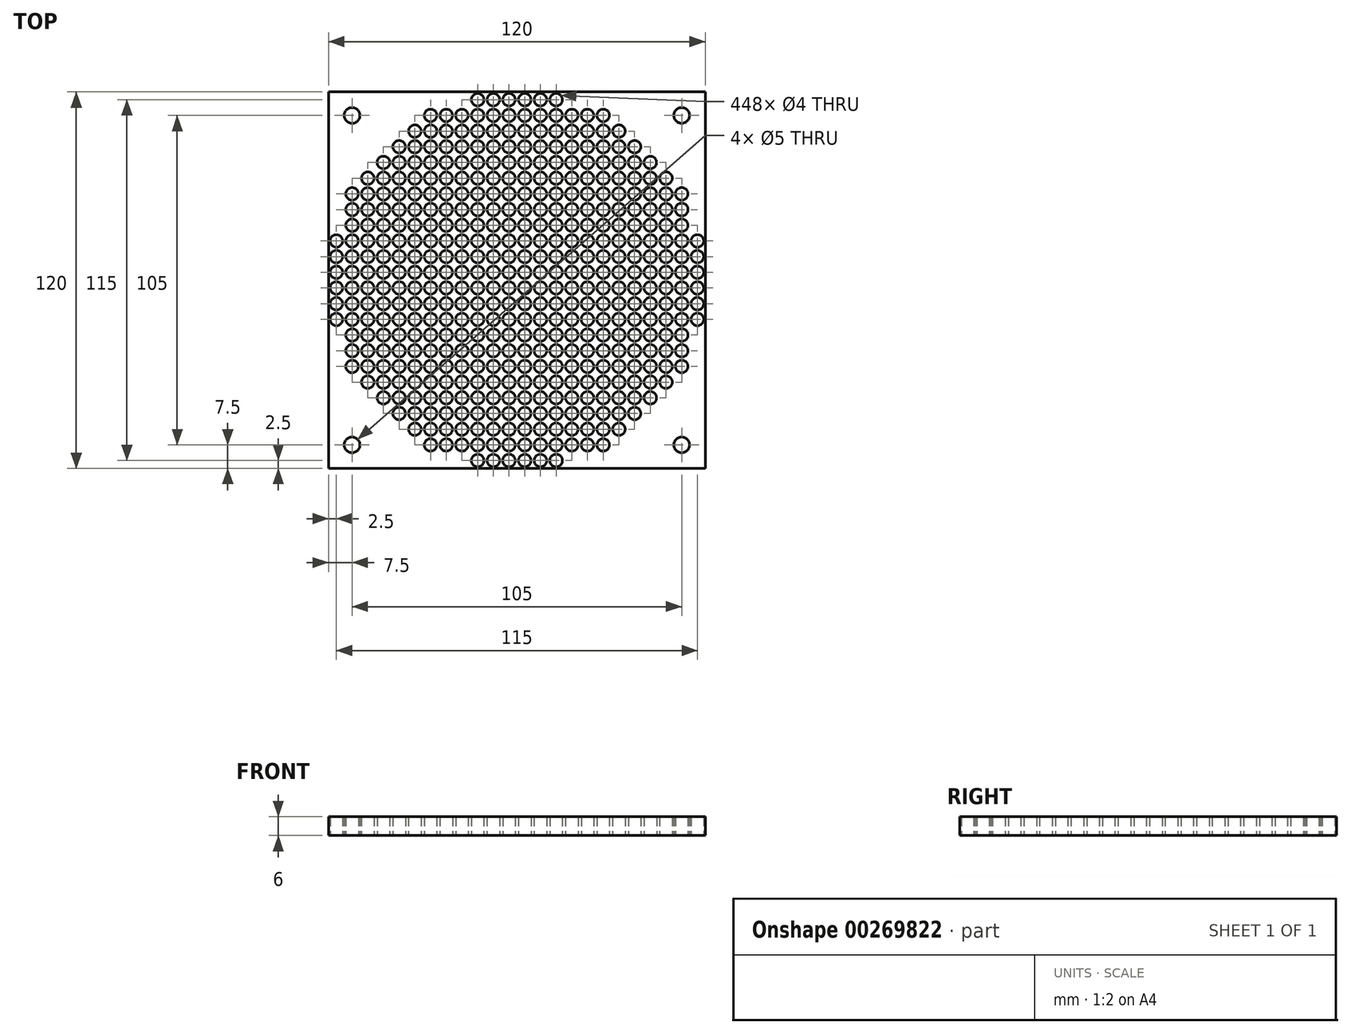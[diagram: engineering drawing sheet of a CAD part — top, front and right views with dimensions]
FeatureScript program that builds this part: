
annotation { "Feature Type Name" : "Feature", "Feature Type Description" : "" }
export const myFeature = defineFeature(function(context is Context, id is Id, definition is map)
    precondition{}
    {
        {
            var Q0;
            Q0=qCreatedBy(makeId("Top.planeOp"),FACE);
            var sketch = newSketch(context, id + "F0", { "sketchPlane" : qUnion([Q0])});
            skLineSegment(sketch, "E0", {"start": v(-60, 60) * mm, "end": v(0, 60) * mm});
            skLineSegment(sketch, "E1", {"start": v(-60, 60) * mm, "end": v(-60, 0) * mm});
            skLineSegment(sketch, "E2.MirrorCS", {"start": v(60, 60) * mm, "end": v(0, 60) * mm});
            skLineSegment(sketch, "E3.MirrorCS", {"start": v(60, 60) * mm, "end": v(60, 0) * mm});
            skLineSegment(sketch, "E4.MirrorCS", {"start": v(-60, -60) * mm, "end": v(-60, 0) * mm});
            skLineSegment(sketch, "E5.MirrorCS", {"start": v(-60, -60) * mm, "end": v(0, -60) * mm});
            skLineSegment(sketch, "E6.MirrorCS", {"start": v(60, -60) * mm, "end": v(0, -60) * mm});
            skLineSegment(sketch, "E7.MirrorCS", {"start": v(60, -60) * mm, "end": v(60, 0) * mm});
            skCircle(sketch, "E8", {"center": v(-52.5, 52.5) * mm, "radius": 2.5 * mm});
            skCircle(sketch, "E9.MirrorC", {"center": v(52.5, 52.5) * mm, "radius": 2.5 * mm});
            skCircle(sketch, "E10.MirrorC", {"center": v(-52.5, -52.5) * mm, "radius": 2.5 * mm});
            skCircle(sketch, "E11.MirrorC", {"center": v(52.5, -52.5) * mm, "radius": 2.5 * mm});
            skCircle(sketch, "E12", {"center": v(-2.5, 2.5) * mm, "radius": 2 * mm});
            skCircle(sketch, "E13.0.1.0", {"center": v(-2.5, 7.5) * mm, "radius": 2 * mm});
            skCircle(sketch, "E13.0.2.0", {"center": v(-2.5, 12.5) * mm, "radius": 2 * mm});
            skCircle(sketch, "E13.0.3.0", {"center": v(-2.5, 17.5) * mm, "radius": 2 * mm});
            skCircle(sketch, "E13.0.4.0", {"center": v(-2.5, 22.5) * mm, "radius": 2 * mm});
            skCircle(sketch, "E13.0.5.0", {"center": v(-2.5, 27.5) * mm, "radius": 2 * mm});
            skCircle(sketch, "E13.0.6.0", {"center": v(-2.5, 32.5) * mm, "radius": 2 * mm});
            skCircle(sketch, "E13.0.7.0", {"center": v(-2.5, 37.5) * mm, "radius": 2 * mm});
            skCircle(sketch, "E13.0.8.0", {"center": v(-2.5, 42.5) * mm, "radius": 2 * mm});
            skCircle(sketch, "E13.0.9.0", {"center": v(-2.5, 47.5) * mm, "radius": 2 * mm});
            skCircle(sketch, "E13.0.10.0", {"center": v(-2.5, 52.5) * mm, "radius": 2 * mm});
            skCircle(sketch, "E13.0.11.0", {"center": v(-2.5, 57.5) * mm, "radius": 2 * mm});
            skCircle(sketch, "E13.1.0.0", {"center": v(-7.5, 2.5) * mm, "radius": 2 * mm});
            skCircle(sketch, "E13.1.1.0", {"center": v(-7.5, 7.5) * mm, "radius": 2 * mm});
            skCircle(sketch, "E13.1.2.0", {"center": v(-7.5, 12.5) * mm, "radius": 2 * mm});
            skCircle(sketch, "E13.1.3.0", {"center": v(-7.5, 17.5) * mm, "radius": 2 * mm});
            skCircle(sketch, "E13.1.4.0", {"center": v(-7.5, 22.5) * mm, "radius": 2 * mm});
            skCircle(sketch, "E13.1.5.0", {"center": v(-7.5, 27.5) * mm, "radius": 2 * mm});
            skCircle(sketch, "E13.1.6.0", {"center": v(-7.5, 32.5) * mm, "radius": 2 * mm});
            skCircle(sketch, "E13.1.7.0", {"center": v(-7.5, 37.5) * mm, "radius": 2 * mm});
            skCircle(sketch, "E13.1.8.0", {"center": v(-7.5, 42.5) * mm, "radius": 2 * mm});
            skCircle(sketch, "E13.1.9.0", {"center": v(-7.5, 47.5) * mm, "radius": 2 * mm});
            skCircle(sketch, "E13.1.10.0", {"center": v(-7.5, 52.5) * mm, "radius": 2 * mm});
            skCircle(sketch, "E13.1.11.0", {"center": v(-7.5, 57.5) * mm, "radius": 2 * mm});
            skCircle(sketch, "E13.2.0.0", {"center": v(-12.5, 2.5) * mm, "radius": 2 * mm});
            skCircle(sketch, "E13.2.1.0", {"center": v(-12.5, 7.5) * mm, "radius": 2 * mm});
            skCircle(sketch, "E13.2.2.0", {"center": v(-12.5, 12.5) * mm, "radius": 2 * mm});
            skCircle(sketch, "E13.2.3.0", {"center": v(-12.5, 17.5) * mm, "radius": 2 * mm});
            skCircle(sketch, "E13.2.4.0", {"center": v(-12.5, 22.5) * mm, "radius": 2 * mm});
            skCircle(sketch, "E13.2.5.0", {"center": v(-12.5, 27.5) * mm, "radius": 2 * mm});
            skCircle(sketch, "E13.2.6.0", {"center": v(-12.5, 32.5) * mm, "radius": 2 * mm});
            skCircle(sketch, "E13.2.7.0", {"center": v(-12.5, 37.5) * mm, "radius": 2 * mm});
            skCircle(sketch, "E13.2.8.0", {"center": v(-12.5, 42.5) * mm, "radius": 2 * mm});
            skCircle(sketch, "E13.2.9.0", {"center": v(-12.5, 47.5) * mm, "radius": 2 * mm});
            skCircle(sketch, "E13.2.10.0", {"center": v(-12.5, 52.5) * mm, "radius": 2 * mm});
            skCircle(sketch, "E13.2.11.0", {"center": v(-12.5, 57.5) * mm, "radius": 2 * mm});
            skCircle(sketch, "E13.3.0.0", {"center": v(-17.5, 2.5) * mm, "radius": 2 * mm});
            skCircle(sketch, "E13.3.1.0", {"center": v(-17.5, 7.5) * mm, "radius": 2 * mm});
            skCircle(sketch, "E13.3.2.0", {"center": v(-17.5, 12.5) * mm, "radius": 2 * mm});
            skCircle(sketch, "E13.3.3.0", {"center": v(-17.5, 17.5) * mm, "radius": 2 * mm});
            skCircle(sketch, "E13.3.4.0", {"center": v(-17.5, 22.5) * mm, "radius": 2 * mm});
            skCircle(sketch, "E13.3.5.0", {"center": v(-17.5, 27.5) * mm, "radius": 2 * mm});
            skCircle(sketch, "E13.3.6.0", {"center": v(-17.5, 32.5) * mm, "radius": 2 * mm});
            skCircle(sketch, "E13.3.7.0", {"center": v(-17.5, 37.5) * mm, "radius": 2 * mm});
            skCircle(sketch, "E13.3.8.0", {"center": v(-17.5, 42.5) * mm, "radius": 2 * mm});
            skCircle(sketch, "E13.3.9.0", {"center": v(-17.5, 47.5) * mm, "radius": 2 * mm});
            skCircle(sketch, "E13.3.10.0", {"center": v(-17.5, 52.5) * mm, "radius": 2 * mm});
            skCircle(sketch, "E13.4.0.0", {"center": v(-22.5, 2.5) * mm, "radius": 2 * mm});
            skCircle(sketch, "E13.4.1.0", {"center": v(-22.5, 7.5) * mm, "radius": 2 * mm});
            skCircle(sketch, "E13.4.2.0", {"center": v(-22.5, 12.5) * mm, "radius": 2 * mm});
            skCircle(sketch, "E13.4.3.0", {"center": v(-22.5, 17.5) * mm, "radius": 2 * mm});
            skCircle(sketch, "E13.4.4.0", {"center": v(-22.5, 22.5) * mm, "radius": 2 * mm});
            skCircle(sketch, "E13.4.5.0", {"center": v(-22.5, 27.5) * mm, "radius": 2 * mm});
            skCircle(sketch, "E13.4.6.0", {"center": v(-22.5, 32.5) * mm, "radius": 2 * mm});
            skCircle(sketch, "E13.4.7.0", {"center": v(-22.5, 37.5) * mm, "radius": 2 * mm});
            skCircle(sketch, "E13.4.8.0", {"center": v(-22.5, 42.5) * mm, "radius": 2 * mm});
            skCircle(sketch, "E13.4.9.0", {"center": v(-22.5, 47.5) * mm, "radius": 2 * mm});
            skCircle(sketch, "E13.4.10.0", {"center": v(-22.5, 52.5) * mm, "radius": 2 * mm});
            skCircle(sketch, "E13.5.0.0", {"center": v(-27.5, 2.5) * mm, "radius": 2 * mm});
            skCircle(sketch, "E13.5.1.0", {"center": v(-27.5, 7.5) * mm, "radius": 2 * mm});
            skCircle(sketch, "E13.5.2.0", {"center": v(-27.5, 12.5) * mm, "radius": 2 * mm});
            skCircle(sketch, "E13.5.3.0", {"center": v(-27.5, 17.5) * mm, "radius": 2 * mm});
            skCircle(sketch, "E13.5.4.0", {"center": v(-27.5, 22.5) * mm, "radius": 2 * mm});
            skCircle(sketch, "E13.5.5.0", {"center": v(-27.5, 27.5) * mm, "radius": 2 * mm});
            skCircle(sketch, "E13.5.6.0", {"center": v(-27.5, 32.5) * mm, "radius": 2 * mm});
            skCircle(sketch, "E13.5.7.0", {"center": v(-27.5, 37.5) * mm, "radius": 2 * mm});
            skCircle(sketch, "E13.5.8.0", {"center": v(-27.5, 42.5) * mm, "radius": 2 * mm});
            skCircle(sketch, "E13.5.9.0", {"center": v(-27.5, 47.5) * mm, "radius": 2 * mm});
            skCircle(sketch, "E13.5.10.0", {"center": v(-27.5, 52.5) * mm, "radius": 2 * mm});
            skCircle(sketch, "E13.6.0.0", {"center": v(-32.5, 2.5) * mm, "radius": 2 * mm});
            skCircle(sketch, "E13.6.1.0", {"center": v(-32.5, 7.5) * mm, "radius": 2 * mm});
            skCircle(sketch, "E13.6.2.0", {"center": v(-32.5, 12.5) * mm, "radius": 2 * mm});
            skCircle(sketch, "E13.6.3.0", {"center": v(-32.5, 17.5) * mm, "radius": 2 * mm});
            skCircle(sketch, "E13.6.4.0", {"center": v(-32.5, 22.5) * mm, "radius": 2 * mm});
            skCircle(sketch, "E13.6.5.0", {"center": v(-32.5, 27.5) * mm, "radius": 2 * mm});
            skCircle(sketch, "E13.6.6.0", {"center": v(-32.5, 32.5) * mm, "radius": 2 * mm});
            skCircle(sketch, "E13.6.7.0", {"center": v(-32.5, 37.5) * mm, "radius": 2 * mm});
            skCircle(sketch, "E13.6.8.0", {"center": v(-32.5, 42.5) * mm, "radius": 2 * mm});
            skCircle(sketch, "E13.6.9.0", {"center": v(-32.5, 47.5) * mm, "radius": 2 * mm});
            skCircle(sketch, "E13.7.0.0", {"center": v(-37.5, 2.5) * mm, "radius": 2 * mm});
            skCircle(sketch, "E13.7.1.0", {"center": v(-37.5, 7.5) * mm, "radius": 2 * mm});
            skCircle(sketch, "E13.7.2.0", {"center": v(-37.5, 12.5) * mm, "radius": 2 * mm});
            skCircle(sketch, "E13.7.3.0", {"center": v(-37.5, 17.5) * mm, "radius": 2 * mm});
            skCircle(sketch, "E13.7.4.0", {"center": v(-37.5, 22.5) * mm, "radius": 2 * mm});
            skCircle(sketch, "E13.7.5.0", {"center": v(-37.5, 27.5) * mm, "radius": 2 * mm});
            skCircle(sketch, "E13.7.6.0", {"center": v(-37.5, 32.5) * mm, "radius": 2 * mm});
            skCircle(sketch, "E13.7.7.0", {"center": v(-37.5, 37.5) * mm, "radius": 2 * mm});
            skCircle(sketch, "E13.7.8.0", {"center": v(-37.5, 42.5) * mm, "radius": 2 * mm});
            skCircle(sketch, "E13.8.0.0", {"center": v(-42.5, 2.5) * mm, "radius": 2 * mm});
            skCircle(sketch, "E13.8.1.0", {"center": v(-42.5, 7.5) * mm, "radius": 2 * mm});
            skCircle(sketch, "E13.8.2.0", {"center": v(-42.5, 12.5) * mm, "radius": 2 * mm});
            skCircle(sketch, "E13.8.3.0", {"center": v(-42.5, 17.5) * mm, "radius": 2 * mm});
            skCircle(sketch, "E13.8.4.0", {"center": v(-42.5, 22.5) * mm, "radius": 2 * mm});
            skCircle(sketch, "E13.8.5.0", {"center": v(-42.5, 27.5) * mm, "radius": 2 * mm});
            skCircle(sketch, "E13.8.6.0", {"center": v(-42.5, 32.5) * mm, "radius": 2 * mm});
            skCircle(sketch, "E13.8.7.0", {"center": v(-42.5, 37.5) * mm, "radius": 2 * mm});
            skCircle(sketch, "E13.9.0.0", {"center": v(-47.5, 2.5) * mm, "radius": 2 * mm});
            skCircle(sketch, "E13.9.1.0", {"center": v(-47.5, 7.5) * mm, "radius": 2 * mm});
            skCircle(sketch, "E13.9.2.0", {"center": v(-47.5, 12.5) * mm, "radius": 2 * mm});
            skCircle(sketch, "E13.9.3.0", {"center": v(-47.5, 17.5) * mm, "radius": 2 * mm});
            skCircle(sketch, "E13.9.4.0", {"center": v(-47.5, 22.5) * mm, "radius": 2 * mm});
            skCircle(sketch, "E13.9.5.0", {"center": v(-47.5, 27.5) * mm, "radius": 2 * mm});
            skCircle(sketch, "E13.9.6.0", {"center": v(-47.5, 32.5) * mm, "radius": 2 * mm});
            skCircle(sketch, "E13.10.0.0", {"center": v(-52.5, 2.5) * mm, "radius": 2 * mm});
            skCircle(sketch, "E13.10.1.0", {"center": v(-52.5, 7.5) * mm, "radius": 2 * mm});
            skCircle(sketch, "E13.10.2.0", {"center": v(-52.5, 12.5) * mm, "radius": 2 * mm});
            skCircle(sketch, "E13.10.3.0", {"center": v(-52.5, 17.5) * mm, "radius": 2 * mm});
            skCircle(sketch, "E13.10.4.0", {"center": v(-52.5, 22.5) * mm, "radius": 2 * mm});
            skCircle(sketch, "E13.10.5.0", {"center": v(-52.5, 27.5) * mm, "radius": 2 * mm});
            skCircle(sketch, "E13.11.0.0", {"center": v(-57.5, 2.5) * mm, "radius": 2 * mm});
            skCircle(sketch, "E13.11.1.0", {"center": v(-57.5, 7.5) * mm, "radius": 2 * mm});
            skCircle(sketch, "E13.11.2.0", {"center": v(-57.5, 12.5) * mm, "radius": 2 * mm});
            skLineSegment(sketch, "E13.direction1", {"start": v(-2.5, 2.5) * mm, "end": v(-7.5, 2.5) * mm, "construction": true});
            skLineSegment(sketch, "E13.direction2", {"start": v(-2.5, 2.5) * mm, "end": v(-2.5, 7.5) * mm, "construction": true});
            skCircle(sketch, "E14", {"center": v(0, 0) * mm, "radius": 60 * mm, "construction": true});
            skLineSegment(sketch, "E15.MirrorCS", {"start": v(2.5, 2.5) * mm, "end": v(2.5, 7.5) * mm, "construction": true});
            skLineSegment(sketch, "E16.MirrorCS", {"start": v(2.5, 2.5) * mm, "end": v(7.5, 2.5) * mm, "construction": true});
            skCircle(sketch, "E17.MirrorC", {"center": v(12.5, 52.5) * mm, "radius": 2 * mm});
            skCircle(sketch, "E18.MirrorC", {"center": v(12.5, 17.5) * mm, "radius": 2 * mm});
            skCircle(sketch, "E19.MirrorC", {"center": v(2.5, 7.5) * mm, "radius": 2 * mm});
            skCircle(sketch, "E20.MirrorC", {"center": v(57.5, 2.5) * mm, "radius": 2 * mm});
            skCircle(sketch, "E21.MirrorC", {"center": v(42.5, 27.5) * mm, "radius": 2 * mm});
            skCircle(sketch, "E22.MirrorC", {"center": v(32.5, 42.5) * mm, "radius": 2 * mm});
            skCircle(sketch, "E23.MirrorC", {"center": v(27.5, 17.5) * mm, "radius": 2 * mm});
            skCircle(sketch, "E24.MirrorC", {"center": v(17.5, 17.5) * mm, "radius": 2 * mm});
            skCircle(sketch, "E25.MirrorC", {"center": v(17.5, 52.5) * mm, "radius": 2 * mm});
            skCircle(sketch, "E26.MirrorC", {"center": v(52.5, 2.5) * mm, "radius": 2 * mm});
            skCircle(sketch, "E27.MirrorC", {"center": v(7.5, 12.5) * mm, "radius": 2 * mm});
            skCircle(sketch, "E28.MirrorC", {"center": v(57.5, 7.5) * mm, "radius": 2 * mm});
            skCircle(sketch, "E29.MirrorC", {"center": v(42.5, 32.5) * mm, "radius": 2 * mm});
            skCircle(sketch, "E30.MirrorC", {"center": v(32.5, 47.5) * mm, "radius": 2 * mm});
            skCircle(sketch, "E31.MirrorC", {"center": v(27.5, 22.5) * mm, "radius": 2 * mm});
            skCircle(sketch, "E32.MirrorC", {"center": v(22.5, 2.5) * mm, "radius": 2 * mm});
            skCircle(sketch, "E33.MirrorC", {"center": v(12.5, 37.5) * mm, "radius": 2 * mm});
            skCircle(sketch, "E34.MirrorC", {"center": v(22.5, 7.5) * mm, "radius": 2 * mm});
            skCircle(sketch, "E35.MirrorC", {"center": v(7.5, 22.5) * mm, "radius": 2 * mm});
            skCircle(sketch, "E36.MirrorC", {"center": v(47.5, 2.5) * mm, "radius": 2 * mm});
            skCircle(sketch, "E37.MirrorC", {"center": v(37.5, 7.5) * mm, "radius": 2 * mm});
            skCircle(sketch, "E38.MirrorC", {"center": v(27.5, 32.5) * mm, "radius": 2 * mm});
            skCircle(sketch, "E39.MirrorC", {"center": v(27.5, 42.5) * mm, "radius": 2 * mm});
            skCircle(sketch, "E40.MirrorC", {"center": v(7.5, 32.5) * mm, "radius": 2 * mm});
            skCircle(sketch, "E41.MirrorC", {"center": v(12.5, 12.5) * mm, "radius": 2 * mm});
            skCircle(sketch, "E42.MirrorC", {"center": v(27.5, 12.5) * mm, "radius": 2 * mm});
            skCircle(sketch, "E43.MirrorC", {"center": v(42.5, 22.5) * mm, "radius": 2 * mm});
            skCircle(sketch, "E44.MirrorC", {"center": v(2.5, 37.5) * mm, "radius": 2 * mm});
            skCircle(sketch, "E45.MirrorC", {"center": v(32.5, 27.5) * mm, "radius": 2 * mm});
            skCircle(sketch, "E46.MirrorC", {"center": v(27.5, 7.5) * mm, "radius": 2 * mm});
            skCircle(sketch, "E47.MirrorC", {"center": v(2.5, 57.5) * mm, "radius": 2 * mm});
            skCircle(sketch, "E48.MirrorC", {"center": v(17.5, 22.5) * mm, "radius": 2 * mm});
            skCircle(sketch, "E49.MirrorC", {"center": v(17.5, 47.5) * mm, "radius": 2 * mm});
            skCircle(sketch, "E50.MirrorC", {"center": v(17.5, 27.5) * mm, "radius": 2 * mm});
            skCircle(sketch, "E51.MirrorC", {"center": v(22.5, 42.5) * mm, "radius": 2 * mm});
            skCircle(sketch, "E52.MirrorC", {"center": v(32.5, 12.5) * mm, "radius": 2 * mm});
            skCircle(sketch, "E53.MirrorC", {"center": v(22.5, 52.5) * mm, "radius": 2 * mm});
            skCircle(sketch, "E54.MirrorC", {"center": v(52.5, 17.5) * mm, "radius": 2 * mm});
            skCircle(sketch, "E55.MirrorC", {"center": v(17.5, 32.5) * mm, "radius": 2 * mm});
            skCircle(sketch, "E56.MirrorC", {"center": v(32.5, 22.5) * mm, "radius": 2 * mm});
            skCircle(sketch, "E57.MirrorC", {"center": v(37.5, 37.5) * mm, "radius": 2 * mm});
            skCircle(sketch, "E58.MirrorC", {"center": v(47.5, 32.5) * mm, "radius": 2 * mm});
            skCircle(sketch, "E59.MirrorC", {"center": v(7.5, 52.5) * mm, "radius": 2 * mm});
            skCircle(sketch, "E60.MirrorC", {"center": v(2.5, 52.5) * mm, "radius": 2 * mm});
            skCircle(sketch, "E61.MirrorC", {"center": v(42.5, 12.5) * mm, "radius": 2 * mm});
            skCircle(sketch, "E62.MirrorC", {"center": v(2.5, 17.5) * mm, "radius": 2 * mm});
            skCircle(sketch, "E63.MirrorC", {"center": v(12.5, 27.5) * mm, "radius": 2 * mm});
            skCircle(sketch, "E64.MirrorC", {"center": v(7.5, 7.5) * mm, "radius": 2 * mm});
            skCircle(sketch, "E65.MirrorC", {"center": v(22.5, 22.5) * mm, "radius": 2 * mm});
            skCircle(sketch, "E66.MirrorC", {"center": v(12.5, 57.5) * mm, "radius": 2 * mm});
            skCircle(sketch, "E67.MirrorC", {"center": v(32.5, 17.5) * mm, "radius": 2 * mm});
            skCircle(sketch, "E68.MirrorC", {"center": v(22.5, 47.5) * mm, "radius": 2 * mm});
            skCircle(sketch, "E69.MirrorC", {"center": v(7.5, 57.5) * mm, "radius": 2 * mm});
            skCircle(sketch, "E70.MirrorC", {"center": v(12.5, 32.5) * mm, "radius": 2 * mm});
            skCircle(sketch, "E71.MirrorC", {"center": v(7.5, 17.5) * mm, "radius": 2 * mm});
            skCircle(sketch, "E72.MirrorC", {"center": v(57.5, 12.5) * mm, "radius": 2 * mm});
            skCircle(sketch, "E73.MirrorC", {"center": v(42.5, 37.5) * mm, "radius": 2 * mm});
            skCircle(sketch, "E74.MirrorC", {"center": v(37.5, 2.5) * mm, "radius": 2 * mm});
            skCircle(sketch, "E75.MirrorC", {"center": v(27.5, 27.5) * mm, "radius": 2 * mm});
            skCircle(sketch, "E76.MirrorC", {"center": v(27.5, 37.5) * mm, "radius": 2 * mm});
            skCircle(sketch, "E77.MirrorC", {"center": v(12.5, 2.5) * mm, "radius": 2 * mm});
            skCircle(sketch, "E78.MirrorC", {"center": v(22.5, 12.5) * mm, "radius": 2 * mm});
            skCircle(sketch, "E79.MirrorC", {"center": v(12.5, 47.5) * mm, "radius": 2 * mm});
            skCircle(sketch, "E80.MirrorC", {"center": v(52.5, 7.5) * mm, "radius": 2 * mm});
            skCircle(sketch, "E81.MirrorC", {"center": v(42.5, 2.5) * mm, "radius": 2 * mm});
            skCircle(sketch, "E82.MirrorC", {"center": v(2.5, 2.5) * mm, "radius": 2 * mm});
            skCircle(sketch, "E83.MirrorC", {"center": v(7.5, 27.5) * mm, "radius": 2 * mm});
            skCircle(sketch, "E84.MirrorC", {"center": v(47.5, 22.5) * mm, "radius": 2 * mm});
            skCircle(sketch, "E85.MirrorC", {"center": v(37.5, 27.5) * mm, "radius": 2 * mm});
            skCircle(sketch, "E86.MirrorC", {"center": v(47.5, 7.5) * mm, "radius": 2 * mm});
            skCircle(sketch, "E87.MirrorC", {"center": v(37.5, 12.5) * mm, "radius": 2 * mm});
            skCircle(sketch, "E88.MirrorC", {"center": v(37.5, 42.5) * mm, "radius": 2 * mm});
            skCircle(sketch, "E89.MirrorC", {"center": v(2.5, 22.5) * mm, "radius": 2 * mm});
            skCircle(sketch, "E90.MirrorC", {"center": v(42.5, 7.5) * mm, "radius": 2 * mm});
            skCircle(sketch, "E91.MirrorC", {"center": v(22.5, 17.5) * mm, "radius": 2 * mm});
            skCircle(sketch, "E92.MirrorC", {"center": v(12.5, 7.5) * mm, "radius": 2 * mm});
            skCircle(sketch, "E93.MirrorC", {"center": v(47.5, 12.5) * mm, "radius": 2 * mm});
            skCircle(sketch, "E94.MirrorC", {"center": v(22.5, 32.5) * mm, "radius": 2 * mm});
            skCircle(sketch, "E95.MirrorC", {"center": v(37.5, 17.5) * mm, "radius": 2 * mm});
            skCircle(sketch, "E96.MirrorC", {"center": v(17.5, 7.5) * mm, "radius": 2 * mm});
            skCircle(sketch, "E97.MirrorC", {"center": v(7.5, 47.5) * mm, "radius": 2 * mm});
            skCircle(sketch, "E98.MirrorC", {"center": v(47.5, 27.5) * mm, "radius": 2 * mm});
            skCircle(sketch, "E99.MirrorC", {"center": v(37.5, 32.5) * mm, "radius": 2 * mm});
            skCircle(sketch, "E100.MirrorC", {"center": v(17.5, 37.5) * mm, "radius": 2 * mm});
            skCircle(sketch, "E101.MirrorC", {"center": v(52.5, 22.5) * mm, "radius": 2 * mm});
            skCircle(sketch, "E102.MirrorC", {"center": v(27.5, 47.5) * mm, "radius": 2 * mm});
            skCircle(sketch, "E103.MirrorC", {"center": v(7.5, 37.5) * mm, "radius": 2 * mm});
            skCircle(sketch, "E104.MirrorC", {"center": v(47.5, 17.5) * mm, "radius": 2 * mm});
            skCircle(sketch, "E105.MirrorC", {"center": v(2.5, 32.5) * mm, "radius": 2 * mm});
            skCircle(sketch, "E106.MirrorC", {"center": v(32.5, 7.5) * mm, "radius": 2 * mm});
            skCircle(sketch, "E107.MirrorC", {"center": v(2.5, 47.5) * mm, "radius": 2 * mm});
            skCircle(sketch, "E108.MirrorC", {"center": v(27.5, 52.5) * mm, "radius": 2 * mm});
            skCircle(sketch, "E109.MirrorC", {"center": v(2.5, 12.5) * mm, "radius": 2 * mm});
            skCircle(sketch, "E110.MirrorC", {"center": v(32.5, 32.5) * mm, "radius": 2 * mm});
            skCircle(sketch, "E111.MirrorC", {"center": v(22.5, 37.5) * mm, "radius": 2 * mm});
            skCircle(sketch, "E112.MirrorC", {"center": v(42.5, 17.5) * mm, "radius": 2 * mm});
            skCircle(sketch, "E113.MirrorC", {"center": v(17.5, 42.5) * mm, "radius": 2 * mm});
            skCircle(sketch, "E114.MirrorC", {"center": v(12.5, 22.5) * mm, "radius": 2 * mm});
            skCircle(sketch, "E115.MirrorC", {"center": v(52.5, 27.5) * mm, "radius": 2 * mm});
            skCircle(sketch, "E116.MirrorC", {"center": v(7.5, 2.5) * mm, "radius": 2 * mm});
            skCircle(sketch, "E117.MirrorC", {"center": v(17.5, 12.5) * mm, "radius": 2 * mm});
            skCircle(sketch, "E118.MirrorC", {"center": v(32.5, 37.5) * mm, "radius": 2 * mm});
            skCircle(sketch, "E119.MirrorC", {"center": v(32.5, 2.5) * mm, "radius": 2 * mm});
            skCircle(sketch, "E120.MirrorC", {"center": v(52.5, 12.5) * mm, "radius": 2 * mm});
            skCircle(sketch, "E121.MirrorC", {"center": v(12.5, 42.5) * mm, "radius": 2 * mm});
            skCircle(sketch, "E122.MirrorC", {"center": v(22.5, 27.5) * mm, "radius": 2 * mm});
            skCircle(sketch, "E123.MirrorC", {"center": v(37.5, 22.5) * mm, "radius": 2 * mm});
            skCircle(sketch, "E124.MirrorC", {"center": v(17.5, 2.5) * mm, "radius": 2 * mm});
            skCircle(sketch, "E125.MirrorC", {"center": v(7.5, 42.5) * mm, "radius": 2 * mm});
            skCircle(sketch, "E126.MirrorC", {"center": v(2.5, 27.5) * mm, "radius": 2 * mm});
            skCircle(sketch, "E127.MirrorC", {"center": v(2.5, 42.5) * mm, "radius": 2 * mm});
            skCircle(sketch, "E128.MirrorC", {"center": v(27.5, 2.5) * mm, "radius": 2 * mm});
            skCircle(sketch, "E129.MirrorC", {"center": v(-2.5, -2.5) * mm, "radius": 2 * mm});
            skLineSegment(sketch, "E130.MirrorCS", {"start": v(2.5, -2.5) * mm, "end": v(2.5, -7.5) * mm, "construction": true});
            skLineSegment(sketch, "E131.MirrorCS", {"start": v(-2.5, -2.5) * mm, "end": v(-2.5, -7.5) * mm, "construction": true});
            skCircle(sketch, "E132.MirrorC", {"center": v(-17.5, -52.5) * mm, "radius": 2 * mm});
            skCircle(sketch, "E133.MirrorC", {"center": v(27.5, -52.5) * mm, "radius": 2 * mm});
            skCircle(sketch, "E134.MirrorC", {"center": v(-27.5, -17.5) * mm, "radius": 2 * mm});
            skCircle(sketch, "E135.MirrorC", {"center": v(-47.5, -2.5) * mm, "radius": 2 * mm});
            skCircle(sketch, "E136.MirrorC", {"center": v(27.5, -7.5) * mm, "radius": 2 * mm});
            skCircle(sketch, "E137.MirrorC", {"center": v(2.5, -17.5) * mm, "radius": 2 * mm});
            skCircle(sketch, "E138.MirrorC", {"center": v(22.5, -32.5) * mm, "radius": 2 * mm});
            skCircle(sketch, "E139.MirrorC", {"center": v(37.5, -12.5) * mm, "radius": 2 * mm});
            skCircle(sketch, "E140.MirrorC", {"center": v(7.5, -37.5) * mm, "radius": 2 * mm});
            skCircle(sketch, "E141.MirrorC", {"center": v(32.5, -2.5) * mm, "radius": 2 * mm});
            skCircle(sketch, "E142.MirrorC", {"center": v(27.5, -17.5) * mm, "radius": 2 * mm});
            skCircle(sketch, "E143.MirrorC", {"center": v(27.5, -42.5) * mm, "radius": 2 * mm});
            skCircle(sketch, "E144.MirrorC", {"center": v(17.5, -32.5) * mm, "radius": 2 * mm});
            skCircle(sketch, "E145.MirrorC", {"center": v(7.5, -17.5) * mm, "radius": 2 * mm});
            skCircle(sketch, "E146.MirrorC", {"center": v(-27.5, -7.5) * mm, "radius": 2 * mm});
            skCircle(sketch, "E147.MirrorC", {"center": v(-32.5, -32.5) * mm, "radius": 2 * mm});
            skCircle(sketch, "E148.MirrorC", {"center": v(-42.5, -17.5) * mm, "radius": 2 * mm});
            skCircle(sketch, "E149.MirrorC", {"center": v(-52.5, -22.5) * mm, "radius": 2 * mm});
            skCircle(sketch, "E150.MirrorC", {"center": v(-2.5, -57.5) * mm, "radius": 2 * mm});
            skCircle(sketch, "E151.MirrorC", {"center": v(-17.5, -37.5) * mm, "radius": 2 * mm});
            skCircle(sketch, "E152.MirrorC", {"center": v(-12.5, -17.5) * mm, "radius": 2 * mm});
            skCircle(sketch, "E153.MirrorC", {"center": v(17.5, -12.5) * mm, "radius": 2 * mm});
            skCircle(sketch, "E154.MirrorC", {"center": v(22.5, -52.5) * mm, "radius": 2 * mm});
            skCircle(sketch, "E155.MirrorC", {"center": v(7.5, -57.5) * mm, "radius": 2 * mm});
            skCircle(sketch, "E156.MirrorC", {"center": v(37.5, -27.5) * mm, "radius": 2 * mm});
            skCircle(sketch, "E157.MirrorC", {"center": v(52.5, -22.5) * mm, "radius": 2 * mm});
            skCircle(sketch, "E158.MirrorC", {"center": v(-27.5, -42.5) * mm, "radius": 2 * mm});
            skCircle(sketch, "E159.MirrorC", {"center": v(-22.5, -7.5) * mm, "radius": 2 * mm});
            skCircle(sketch, "E160.MirrorC", {"center": v(17.5, -52.5) * mm, "radius": 2 * mm});
            skCircle(sketch, "E161.MirrorC", {"center": v(-7.5, -22.5) * mm, "radius": 2 * mm});
            skCircle(sketch, "E162.MirrorC", {"center": v(2.5, -37.5) * mm, "radius": 2 * mm});
            skCircle(sketch, "E163.MirrorC", {"center": v(2.5, -52.5) * mm, "radius": 2 * mm});
            skCircle(sketch, "E164.MirrorC", {"center": v(-27.5, -12.5) * mm, "radius": 2 * mm});
            skCircle(sketch, "E165.MirrorC", {"center": v(17.5, -17.5) * mm, "radius": 2 * mm});
            skCircle(sketch, "E166.MirrorC", {"center": v(57.5, -7.5) * mm, "radius": 2 * mm});
            skCircle(sketch, "E167.MirrorC", {"center": v(17.5, -2.5) * mm, "radius": 2 * mm});
            skCircle(sketch, "E168.MirrorC", {"center": v(-7.5, -52.5) * mm, "radius": 2 * mm});
            skCircle(sketch, "E169.MirrorC", {"center": v(-17.5, -12.5) * mm, "radius": 2 * mm});
            skCircle(sketch, "E170.MirrorC", {"center": v(-22.5, -37.5) * mm, "radius": 2 * mm});
            skCircle(sketch, "E171.MirrorC", {"center": v(12.5, -7.5) * mm, "radius": 2 * mm});
            skCircle(sketch, "E172.MirrorC", {"center": v(42.5, -37.5) * mm, "radius": 2 * mm});
            skCircle(sketch, "E173.MirrorC", {"center": v(-32.5, -7.5) * mm, "radius": 2 * mm});
            skCircle(sketch, "E174.MirrorC", {"center": v(-2.5, -32.5) * mm, "radius": 2 * mm});
            skCircle(sketch, "E175.MirrorC", {"center": v(7.5, -47.5) * mm, "radius": 2 * mm});
            skCircle(sketch, "E176.MirrorC", {"center": v(42.5, -2.5) * mm, "radius": 2 * mm});
            skCircle(sketch, "E177.MirrorC", {"center": v(22.5, -22.5) * mm, "radius": 2 * mm});
            skCircle(sketch, "E178.MirrorC", {"center": v(17.5, -47.5) * mm, "radius": 2 * mm});
            skCircle(sketch, "E179.MirrorC", {"center": v(12.5, -22.5) * mm, "radius": 2 * mm});
            skCircle(sketch, "E180.MirrorC", {"center": v(2.5, -22.5) * mm, "radius": 2 * mm});
            skCircle(sketch, "E181.MirrorC", {"center": v(-22.5, -22.5) * mm, "radius": 2 * mm});
            skCircle(sketch, "E182.MirrorC", {"center": v(-27.5, -47.5) * mm, "radius": 2 * mm});
            skCircle(sketch, "E183.MirrorC", {"center": v(17.5, -42.5) * mm, "radius": 2 * mm});
            skCircle(sketch, "E184.MirrorC", {"center": v(37.5, -42.5) * mm, "radius": 2 * mm});
            skCircle(sketch, "E185.MirrorC", {"center": v(-12.5, -27.5) * mm, "radius": 2 * mm});
            skCircle(sketch, "E186.MirrorC", {"center": v(-2.5, -27.5) * mm, "radius": 2 * mm});
            skCircle(sketch, "E187.MirrorC", {"center": v(2.5, -57.5) * mm, "radius": 2 * mm});
            skCircle(sketch, "E188.MirrorC", {"center": v(22.5, -47.5) * mm, "radius": 2 * mm});
            skCircle(sketch, "E189.MirrorC", {"center": v(42.5, -7.5) * mm, "radius": 2 * mm});
            skCircle(sketch, "E190.MirrorC", {"center": v(7.5, -2.5) * mm, "radius": 2 * mm});
            skCircle(sketch, "E191.MirrorC", {"center": v(12.5, -2.5) * mm, "radius": 2 * mm});
            skCircle(sketch, "E192.MirrorC", {"center": v(42.5, -12.5) * mm, "radius": 2 * mm});
            skCircle(sketch, "E193.MirrorC", {"center": v(2.5, -12.5) * mm, "radius": 2 * mm});
            skCircle(sketch, "E194.MirrorC", {"center": v(-12.5, -22.5) * mm, "radius": 2 * mm});
            skCircle(sketch, "E195.MirrorC", {"center": v(-52.5, -27.5) * mm, "radius": 2 * mm});
            skCircle(sketch, "E196.MirrorC", {"center": v(32.5, -7.5) * mm, "radius": 2 * mm});
            skCircle(sketch, "E197.MirrorC", {"center": v(32.5, -32.5) * mm, "radius": 2 * mm});
            skCircle(sketch, "E198.MirrorC", {"center": v(-42.5, -22.5) * mm, "radius": 2 * mm});
            skCircle(sketch, "E199.MirrorC", {"center": v(57.5, -12.5) * mm, "radius": 2 * mm});
            skCircle(sketch, "E200.MirrorC", {"center": v(32.5, -22.5) * mm, "radius": 2 * mm});
            skCircle(sketch, "E201.MirrorC", {"center": v(-57.5, -12.5) * mm, "radius": 2 * mm});
            skCircle(sketch, "E202.MirrorC", {"center": v(-37.5, -12.5) * mm, "radius": 2 * mm});
            skCircle(sketch, "E203.MirrorC", {"center": v(47.5, -12.5) * mm, "radius": 2 * mm});
            skCircle(sketch, "E204.MirrorC", {"center": v(2.5, -27.5) * mm, "radius": 2 * mm});
            skCircle(sketch, "E205.MirrorC", {"center": v(2.5, -47.5) * mm, "radius": 2 * mm});
            skCircle(sketch, "E206.MirrorC", {"center": v(22.5, -12.5) * mm, "radius": 2 * mm});
            skCircle(sketch, "E207.MirrorC", {"center": v(7.5, -12.5) * mm, "radius": 2 * mm});
            skCircle(sketch, "E208.MirrorC", {"center": v(42.5, -22.5) * mm, "radius": 2 * mm});
            skCircle(sketch, "E209.MirrorC", {"center": v(-37.5, -17.5) * mm, "radius": 2 * mm});
            skCircle(sketch, "E210.MirrorC", {"center": v(-47.5, -12.5) * mm, "radius": 2 * mm});
            skCircle(sketch, "E211.MirrorC", {"center": v(32.5, -47.5) * mm, "radius": 2 * mm});
            skCircle(sketch, "E212.MirrorC", {"center": v(-37.5, -2.5) * mm, "radius": 2 * mm});
            skCircle(sketch, "E213.MirrorC", {"center": v(-42.5, -37.5) * mm, "radius": 2 * mm});
            skCircle(sketch, "E214.MirrorC", {"center": v(-37.5, -22.5) * mm, "radius": 2 * mm});
            skCircle(sketch, "E215.MirrorC", {"center": v(12.5, -47.5) * mm, "radius": 2 * mm});
            skCircle(sketch, "E216.MirrorC", {"center": v(22.5, -2.5) * mm, "radius": 2 * mm});
            skCircle(sketch, "E217.MirrorC", {"center": v(-37.5, -32.5) * mm, "radius": 2 * mm});
            skCircle(sketch, "E218.MirrorC", {"center": v(-47.5, -27.5) * mm, "radius": 2 * mm});
            skCircle(sketch, "E219.MirrorC", {"center": v(12.5, -52.5) * mm, "radius": 2 * mm});
            skCircle(sketch, "E220.MirrorC", {"center": v(12.5, -37.5) * mm, "radius": 2 * mm});
            skCircle(sketch, "E221.MirrorC", {"center": v(-22.5, -17.5) * mm, "radius": 2 * mm});
            skCircle(sketch, "E222.MirrorC", {"center": v(-7.5, -32.5) * mm, "radius": 2 * mm});
            skCircle(sketch, "E223.MirrorC", {"center": v(-57.5, -2.5) * mm, "radius": 2 * mm});
            skCircle(sketch, "E224.MirrorC", {"center": v(-32.5, -2.5) * mm, "radius": 2 * mm});
            skCircle(sketch, "E225.MirrorC", {"center": v(-37.5, -27.5) * mm, "radius": 2 * mm});
            skCircle(sketch, "E226.MirrorC", {"center": v(-17.5, -7.5) * mm, "radius": 2 * mm});
            skCircle(sketch, "E227.MirrorC", {"center": v(-22.5, -32.5) * mm, "radius": 2 * mm});
            skCircle(sketch, "E228.MirrorC", {"center": v(17.5, -7.5) * mm, "radius": 2 * mm});
            skCircle(sketch, "E229.MirrorC", {"center": v(52.5, -7.5) * mm, "radius": 2 * mm});
            skCircle(sketch, "E230.MirrorC", {"center": v(-27.5, -32.5) * mm, "radius": 2 * mm});
            skCircle(sketch, "E231.MirrorC", {"center": v(-37.5, -7.5) * mm, "radius": 2 * mm});
            skLineSegment(sketch, "E232.MirrorCS", {"start": v(2.5, -2.5) * mm, "end": v(7.5, -2.5) * mm, "construction": true});
            skLineSegment(sketch, "E233.MirrorCS", {"start": v(-2.5, -2.5) * mm, "end": v(-7.5, -2.5) * mm, "construction": true});
            skCircle(sketch, "E234.MirrorC", {"center": v(12.5, -12.5) * mm, "radius": 2 * mm});
            skCircle(sketch, "E235.MirrorC", {"center": v(12.5, -42.5) * mm, "radius": 2 * mm});
            skCircle(sketch, "E236.MirrorC", {"center": v(-12.5, -42.5) * mm, "radius": 2 * mm});
            skCircle(sketch, "E237.MirrorC", {"center": v(7.5, -32.5) * mm, "radius": 2 * mm});
            skCircle(sketch, "E238.MirrorC", {"center": v(-7.5, -47.5) * mm, "radius": 2 * mm});
            skCircle(sketch, "E239.MirrorC", {"center": v(-42.5, -27.5) * mm, "radius": 2 * mm});
            skCircle(sketch, "E240.MirrorC", {"center": v(-2.5, -7.5) * mm, "radius": 2 * mm});
            skCircle(sketch, "E241.MirrorC", {"center": v(-7.5, -17.5) * mm, "radius": 2 * mm});
            skCircle(sketch, "E242.MirrorC", {"center": v(-2.5, -12.5) * mm, "radius": 2 * mm});
            skCircle(sketch, "E243.MirrorC", {"center": v(-12.5, -37.5) * mm, "radius": 2 * mm});
            skCircle(sketch, "E244.MirrorC", {"center": v(-2.5, -17.5) * mm, "radius": 2 * mm});
            skCircle(sketch, "E245.MirrorC", {"center": v(-22.5, -2.5) * mm, "radius": 2 * mm});
            skCircle(sketch, "E246.MirrorC", {"center": v(22.5, -37.5) * mm, "radius": 2 * mm});
            skCircle(sketch, "E247.MirrorC", {"center": v(2.5, -42.5) * mm, "radius": 2 * mm});
            skCircle(sketch, "E248.MirrorC", {"center": v(12.5, -27.5) * mm, "radius": 2 * mm});
            skCircle(sketch, "E249.MirrorC", {"center": v(37.5, -17.5) * mm, "radius": 2 * mm});
            skCircle(sketch, "E250.MirrorC", {"center": v(-47.5, -17.5) * mm, "radius": 2 * mm});
            skCircle(sketch, "E251.MirrorC", {"center": v(27.5, -22.5) * mm, "radius": 2 * mm});
            skCircle(sketch, "E252.MirrorC", {"center": v(-27.5, -27.5) * mm, "radius": 2 * mm});
            skCircle(sketch, "E253.MirrorC", {"center": v(-22.5, -27.5) * mm, "radius": 2 * mm});
            skCircle(sketch, "E254.MirrorC", {"center": v(-7.5, -2.5) * mm, "radius": 2 * mm});
            skCircle(sketch, "E255.MirrorC", {"center": v(-12.5, -57.5) * mm, "radius": 2 * mm});
            skCircle(sketch, "E256.MirrorC", {"center": v(27.5, -37.5) * mm, "radius": 2 * mm});
            skCircle(sketch, "E257.MirrorC", {"center": v(37.5, -37.5) * mm, "radius": 2 * mm});
            skCircle(sketch, "E258.MirrorC", {"center": v(-17.5, -42.5) * mm, "radius": 2 * mm});
            skCircle(sketch, "E259.MirrorC", {"center": v(-27.5, -52.5) * mm, "radius": 2 * mm});
            skCircle(sketch, "E260.MirrorC", {"center": v(37.5, -7.5) * mm, "radius": 2 * mm});
            skCircle(sketch, "E261.MirrorC", {"center": v(-22.5, -52.5) * mm, "radius": 2 * mm});
            skCircle(sketch, "E262.MirrorC", {"center": v(-32.5, -37.5) * mm, "radius": 2 * mm});
            skCircle(sketch, "E263.MirrorC", {"center": v(22.5, -7.5) * mm, "radius": 2 * mm});
            skCircle(sketch, "E264.MirrorC", {"center": v(-7.5, -42.5) * mm, "radius": 2 * mm});
            skCircle(sketch, "E265.MirrorC", {"center": v(-2.5, -22.5) * mm, "radius": 2 * mm});
            skCircle(sketch, "E266.MirrorC", {"center": v(-12.5, -52.5) * mm, "radius": 2 * mm});
            skCircle(sketch, "E267.MirrorC", {"center": v(32.5, -12.5) * mm, "radius": 2 * mm});
            skCircle(sketch, "E268.MirrorC", {"center": v(47.5, -22.5) * mm, "radius": 2 * mm});
            skCircle(sketch, "E269.MirrorC", {"center": v(17.5, -37.5) * mm, "radius": 2 * mm});
            skCircle(sketch, "E270.MirrorC", {"center": v(32.5, -37.5) * mm, "radius": 2 * mm});
            skCircle(sketch, "E271.MirrorC", {"center": v(-42.5, -2.5) * mm, "radius": 2 * mm});
            skCircle(sketch, "E272.MirrorC", {"center": v(-52.5, -7.5) * mm, "radius": 2 * mm});
            skCircle(sketch, "E273.MirrorC", {"center": v(57.5, -2.5) * mm, "radius": 2 * mm});
            skCircle(sketch, "E274.MirrorC", {"center": v(12.5, -32.5) * mm, "radius": 2 * mm});
            skCircle(sketch, "E275.MirrorC", {"center": v(22.5, -27.5) * mm, "radius": 2 * mm});
            skCircle(sketch, "E276.MirrorC", {"center": v(52.5, -2.5) * mm, "radius": 2 * mm});
            skCircle(sketch, "E277.MirrorC", {"center": v(47.5, -2.5) * mm, "radius": 2 * mm});
            skCircle(sketch, "E278.MirrorC", {"center": v(-12.5, -2.5) * mm, "radius": 2 * mm});
            skCircle(sketch, "E279.MirrorC", {"center": v(-17.5, -22.5) * mm, "radius": 2 * mm});
            skCircle(sketch, "E280.MirrorC", {"center": v(47.5, -7.5) * mm, "radius": 2 * mm});
            skCircle(sketch, "E281.MirrorC", {"center": v(52.5, -17.5) * mm, "radius": 2 * mm});
            skCircle(sketch, "E282.MirrorC", {"center": v(27.5, -47.5) * mm, "radius": 2 * mm});
            skCircle(sketch, "E283.MirrorC", {"center": v(-42.5, -12.5) * mm, "radius": 2 * mm});
            skCircle(sketch, "E284.MirrorC", {"center": v(-52.5, -17.5) * mm, "radius": 2 * mm});
            skCircle(sketch, "E285.MirrorC", {"center": v(-22.5, -47.5) * mm, "radius": 2 * mm});
            skCircle(sketch, "E286.MirrorC", {"center": v(27.5, -12.5) * mm, "radius": 2 * mm});
            skCircle(sketch, "E287.MirrorC", {"center": v(47.5, -32.5) * mm, "radius": 2 * mm});
            skCircle(sketch, "E288.MirrorC", {"center": v(-32.5, -17.5) * mm, "radius": 2 * mm});
            skCircle(sketch, "E289.MirrorC", {"center": v(-37.5, -37.5) * mm, "radius": 2 * mm});
            skCircle(sketch, "E290.MirrorC", {"center": v(2.5, -2.5) * mm, "radius": 2 * mm});
            skCircle(sketch, "E291.MirrorC", {"center": v(47.5, -27.5) * mm, "radius": 2 * mm});
            skCircle(sketch, "E292.MirrorC", {"center": v(12.5, -57.5) * mm, "radius": 2 * mm});
            skCircle(sketch, "E293.MirrorC", {"center": v(17.5, -27.5) * mm, "radius": 2 * mm});
            skCircle(sketch, "E294.MirrorC", {"center": v(32.5, -42.5) * mm, "radius": 2 * mm});
            skCircle(sketch, "E295.MirrorC", {"center": v(27.5, -32.5) * mm, "radius": 2 * mm});
            skCircle(sketch, "E296.MirrorC", {"center": v(-2.5, -42.5) * mm, "radius": 2 * mm});
            skCircle(sketch, "E297.MirrorC", {"center": v(-12.5, -12.5) * mm, "radius": 2 * mm});
            skCircle(sketch, "E298.MirrorC", {"center": v(7.5, -42.5) * mm, "radius": 2 * mm});
            skCircle(sketch, "E299.MirrorC", {"center": v(32.5, -27.5) * mm, "radius": 2 * mm});
            skCircle(sketch, "E300.MirrorC", {"center": v(42.5, -17.5) * mm, "radius": 2 * mm});
            skCircle(sketch, "E301.MirrorC", {"center": v(-17.5, -32.5) * mm, "radius": 2 * mm});
            skCircle(sketch, "E302.MirrorC", {"center": v(-27.5, -2.5) * mm, "radius": 2 * mm});
            skCircle(sketch, "E303.MirrorC", {"center": v(-32.5, -27.5) * mm, "radius": 2 * mm});
            skCircle(sketch, "E304.MirrorC", {"center": v(37.5, -2.5) * mm, "radius": 2 * mm});
            skCircle(sketch, "E305.MirrorC", {"center": v(-27.5, -22.5) * mm, "radius": 2 * mm});
            skCircle(sketch, "E306.MirrorC", {"center": v(-32.5, -47.5) * mm, "radius": 2 * mm});
            skCircle(sketch, "E307.MirrorC", {"center": v(-7.5, -37.5) * mm, "radius": 2 * mm});
            skCircle(sketch, "E308.MirrorC", {"center": v(-42.5, -32.5) * mm, "radius": 2 * mm});
            skCircle(sketch, "E309.MirrorC", {"center": v(-42.5, -7.5) * mm, "radius": 2 * mm});
            skCircle(sketch, "E310.MirrorC", {"center": v(-47.5, -22.5) * mm, "radius": 2 * mm});
            skCircle(sketch, "E311.MirrorC", {"center": v(-2.5, -52.5) * mm, "radius": 2 * mm});
            skCircle(sketch, "E312.MirrorC", {"center": v(-52.5, -12.5) * mm, "radius": 2 * mm});
            skCircle(sketch, "E313.MirrorC", {"center": v(-12.5, -47.5) * mm, "radius": 2 * mm});
            skCircle(sketch, "E314.MirrorC", {"center": v(-37.5, -42.5) * mm, "radius": 2 * mm});
            skCircle(sketch, "E315.MirrorC", {"center": v(42.5, -27.5) * mm, "radius": 2 * mm});
            skCircle(sketch, "E316.MirrorC", {"center": v(-22.5, -12.5) * mm, "radius": 2 * mm});
            skCircle(sketch, "E317.MirrorC", {"center": v(-12.5, -7.5) * mm, "radius": 2 * mm});
            skCircle(sketch, "E318.MirrorC", {"center": v(27.5, -2.5) * mm, "radius": 2 * mm});
            skCircle(sketch, "E319.MirrorC", {"center": v(-17.5, -27.5) * mm, "radius": 2 * mm});
            skCircle(sketch, "E320.MirrorC", {"center": v(-52.5, -2.5) * mm, "radius": 2 * mm});
            skCircle(sketch, "E321.MirrorC", {"center": v(2.5, -7.5) * mm, "radius": 2 * mm});
            skCircle(sketch, "E322.MirrorC", {"center": v(-27.5, -37.5) * mm, "radius": 2 * mm});
            skCircle(sketch, "E323.MirrorC", {"center": v(7.5, -22.5) * mm, "radius": 2 * mm});
            skCircle(sketch, "E324.MirrorC", {"center": v(22.5, -17.5) * mm, "radius": 2 * mm});
            skCircle(sketch, "E325.MirrorC", {"center": v(37.5, -22.5) * mm, "radius": 2 * mm});
            skCircle(sketch, "E326.MirrorC", {"center": v(7.5, -52.5) * mm, "radius": 2 * mm});
            skCircle(sketch, "E327.MirrorC", {"center": v(-32.5, -22.5) * mm, "radius": 2 * mm});
            skCircle(sketch, "E328.MirrorC", {"center": v(-32.5, -42.5) * mm, "radius": 2 * mm});
            skCircle(sketch, "E329.MirrorC", {"center": v(-7.5, -7.5) * mm, "radius": 2 * mm});
            skCircle(sketch, "E330.MirrorC", {"center": v(-17.5, -47.5) * mm, "radius": 2 * mm});
            skCircle(sketch, "E331.MirrorC", {"center": v(47.5, -17.5) * mm, "radius": 2 * mm});
            skCircle(sketch, "E332.MirrorC", {"center": v(-2.5, -47.5) * mm, "radius": 2 * mm});
            skCircle(sketch, "E333.MirrorC", {"center": v(-7.5, -57.5) * mm, "radius": 2 * mm});
            skCircle(sketch, "E334.MirrorC", {"center": v(-17.5, -17.5) * mm, "radius": 2 * mm});
            skCircle(sketch, "E335.MirrorC", {"center": v(-22.5, -42.5) * mm, "radius": 2 * mm});
            skCircle(sketch, "E336.MirrorC", {"center": v(-32.5, -12.5) * mm, "radius": 2 * mm});
            skCircle(sketch, "E337.MirrorC", {"center": v(-2.5, -37.5) * mm, "radius": 2 * mm});
            skCircle(sketch, "E338.MirrorC", {"center": v(17.5, -22.5) * mm, "radius": 2 * mm});
            skCircle(sketch, "E339.MirrorC", {"center": v(7.5, -7.5) * mm, "radius": 2 * mm});
            skCircle(sketch, "E340.MirrorC", {"center": v(-7.5, -12.5) * mm, "radius": 2 * mm});
            skCircle(sketch, "E341.MirrorC", {"center": v(-57.5, -7.5) * mm, "radius": 2 * mm});
            skCircle(sketch, "E342.MirrorC", {"center": v(27.5, -27.5) * mm, "radius": 2 * mm});
            skCircle(sketch, "E343.MirrorC", {"center": v(52.5, -12.5) * mm, "radius": 2 * mm});
            skCircle(sketch, "E344.MirrorC", {"center": v(-17.5, -2.5) * mm, "radius": 2 * mm});
            skCircle(sketch, "E345.MirrorC", {"center": v(37.5, -32.5) * mm, "radius": 2 * mm});
            skCircle(sketch, "E346.MirrorC", {"center": v(12.5, -17.5) * mm, "radius": 2 * mm});
            skCircle(sketch, "E347.MirrorC", {"center": v(-47.5, -32.5) * mm, "radius": 2 * mm});
            skCircle(sketch, "E348.MirrorC", {"center": v(-47.5, -7.5) * mm, "radius": 2 * mm});
            skCircle(sketch, "E349.MirrorC", {"center": v(-12.5, -32.5) * mm, "radius": 2 * mm});
            skCircle(sketch, "E350.MirrorC", {"center": v(7.5, -27.5) * mm, "radius": 2 * mm});
            skCircle(sketch, "E351.MirrorC", {"center": v(32.5, -17.5) * mm, "radius": 2 * mm});
            skCircle(sketch, "E352.MirrorC", {"center": v(42.5, -32.5) * mm, "radius": 2 * mm});
            skCircle(sketch, "E353.MirrorC", {"center": v(52.5, -27.5) * mm, "radius": 2 * mm});
            skCircle(sketch, "E354.MirrorC", {"center": v(-7.5, -27.5) * mm, "radius": 2 * mm});
            skCircle(sketch, "E355.MirrorC", {"center": v(2.5, -32.5) * mm, "radius": 2 * mm});
            skCircle(sketch, "E356.MirrorC", {"center": v(22.5, -42.5) * mm, "radius": 2 * mm});
            skSolve(sketch);
        }
        {
            var Q0;
            Q0 = qSketchRegion(id + "F0", true);
            extrude(context, id + "F1", {"entities" : qUnion([Q0]), "depth" : 6 * mm, "offsetDistance" : 25 * mm});
        }
    });
